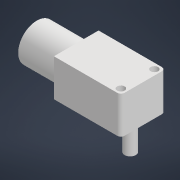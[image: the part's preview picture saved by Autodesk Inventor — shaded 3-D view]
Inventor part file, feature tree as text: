
AUTODESK INVENTOR PART (.ipt)
format: ipt  version: 2022 (Build 260153000, 153)  size: 130,560 bytes
history: native  units: mm
features: sketch x4, extrude x3, fillet x1, hole x1, projected_geometry x1
ambient origin geometry x8: Origin, YZ Plane, XZ Plane, XY Plane, X Axis, Y Axis, Z Axis, Center Point
bodies: Solid1 (feature_tree)
feature tree (10):
  extrude  "Extrusion1"  Depth=8.0mm TaperAngle=0.0deg
  extrude  "Extrusion2"  Depth=12.0mm
  extrude  "Extrusion3"  Depth=10.0mm TaperAngle=0.0deg
  fillet  "Fillet1"  Radius=10.0mm
  hole  "Hole1"  [1 undecoded]
  sketch  "Sketch1"  dims[d0=3.0mm d1=8.0mm d2=0.0mm]
  sketch  "Sketch2"  dims[d3=18.0mm d4=12.0mm]
  sketch  "Sketch3"  dims[d5=3.5mm d6=10.0mm d7=0.0mm d8=10.0mm]
  projected_geometry  "Projected Loop1"
  sketch  "Sketch4"  dims[d9=10.6mm d10=0.0mm d11=1.0mm d12=1.5mm d13=1.5mm d14=1.5mm d15=2.0mm d16=8.0mm d17=4.0mm d18=2.0mm d19=90.0deg d20=12.0mm d21=20.594885mm]
note: 1 required parameter value undecoded (feature->parameter linkage not recoverable at this tier; creation-order binding heuristic only, values carry confidence <= 0.55)
